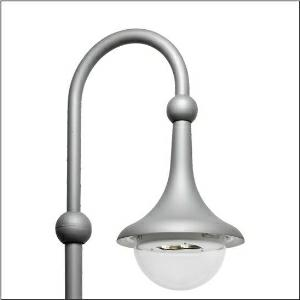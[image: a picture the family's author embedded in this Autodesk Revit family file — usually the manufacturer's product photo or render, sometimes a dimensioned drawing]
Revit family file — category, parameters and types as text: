
# Revit family: grosse_glocke_iq___p1_0a_5xa1565f1f108_f8af
name_source: partatom
category: Lighting Fixtures
units: mm (PartAtom-declared; Revit-internal decimal feet)

## family parameters
Cut with Voids When Loaded = No
Host = Face
Light Source = No
Part Type = Normal
Room Calculation Point = No
Round Connector Dimension = Use Diameter
Shared = No

## types (1)
- --- (1 x LED, 5070 lm, 34.3 W, 3000K)
    Apparent Load = 34 VA
    CIE Flux Codes = 26 57 90 99 100
    Color Rendering = 70
    Color Temperature = 3000K
    Default Elevation = 1800 mm
    Description = Large Bell iQ, mast luminaire, primary light control with 3 zone facetted reflector, of plastic, silver coated, primary optical cover: enclosure, of PMMA, transparent, light distribution: P1.0a, light emission: direct distribution, primary light characteristic: asymmetric, installation type: suspended mounting, High Power LED, rated luminous flux: 5.070lm, luminous efficacy: 148lm/W, light colour: 730, colour temperature: 3000K, control gear: iQ Street-Remote, control: optimised constant luminous flux control (CLO 2.0), Desk-Remote (wireless, voltage-free reading and setting of iQ features in the workshop via application-optimized NFC function/RFID function), Light-Fading, Smart-Wire, Night-Set, Lumen-Switch, Temp-Guard, Auto-Match, Street-Remote, pre-setting: logarithmic dimming characteristic, mains connection: 230..240V, AC, 50/60Hz, start of lifetime: 34W, end of service life: 38W, reduction: 16W, luminaire housing, bell-shaped, of glass-fibre reinforced polyester, coated, Siteco® metallic grey (DB 702S), please order curved mast extension separately, diameter: 530mm, height: 695mm, mounting height: 4..6m, protection rating (complete): IP54, insulation class (complete): insulation class II (safety insulation), certification: CE, ENEC, VDE, impact resistance: IK08, standard-compliant lighting for roads and squares, packaging unit: 1 piece

Light Distribution: P1.0a
    Height = 695 mm
    Lamp = 1 x LED
    Lamp Light Flux = 5070 lm
    Lamp Power = 34.3 W
    Lamp count = 1
    Length = 530 mm
    Luminous efficacy = 148 lm/W
    Manufacturer = Siteco
    ModVariant = No
    Model = 5XA1565F1F108
    Number of Poles = 1
    OnlyDefault = Yes
    Power Factor = 1
    Product Name = Große Glocke iQ | P1.0a
    Product group = mast luminaire | pylon annexe
    ProductGroupID = 6201
    Protection Class = Protection class II
    Protection Degree = IP 54
    RLX_Detail_Level = 1
    RLX_Emergency_Light_Flux = 0 lm
    RLX_Emergency_Type = 0
    RLX_Emergency_Type_DB = No
    RlxData = <blob elided: 53405 chars, md5=326e858a>
    Socket = socket
    Standby Power = 0 W
    System Light Flux = 5070 lm
    System Power = 34 W
    Type Comments = factory setting: luminous flux: 100 % | dim-lin: 254 | 640 mA
    Type Image = l_1347688.jpg
    URL = http://relux.com
    VarID = @adj_059474
    Voltage = 0 V
    Weight = 0.00 kg
    Width = 0 mm  [stored 0 ft]

note: [stored X ft] marks values corroborated as IEEE doubles in the binary element streams (Revit-internal decimal feet)

## geometry (parser evidence)
native form markers: Blend x4, Sweep x8
no freeform markers — native parametric forms only
